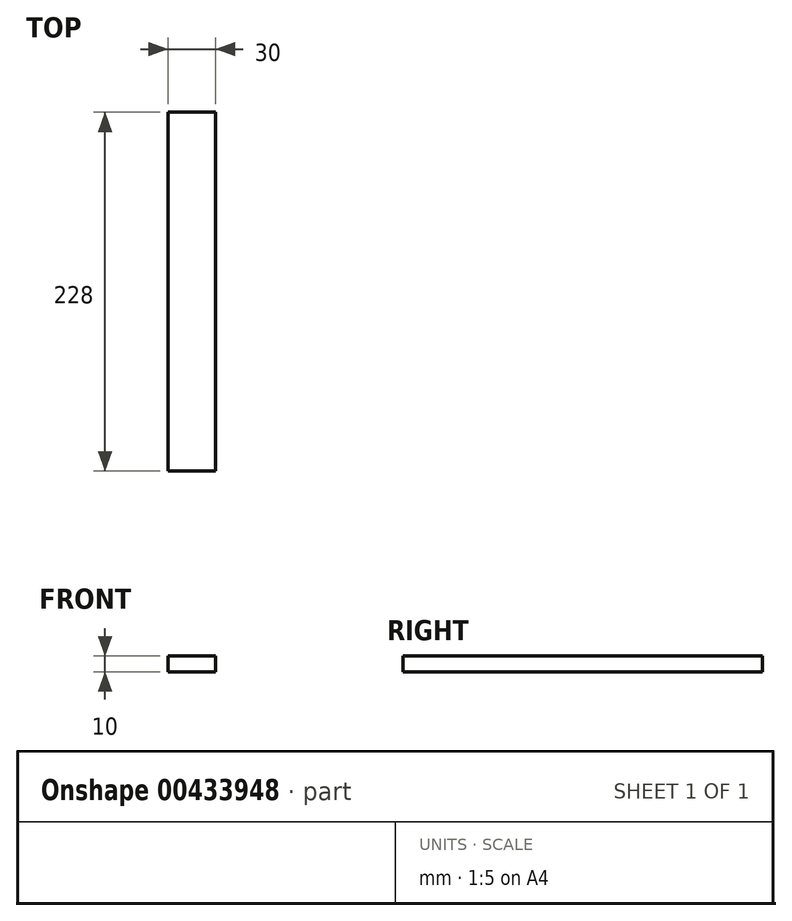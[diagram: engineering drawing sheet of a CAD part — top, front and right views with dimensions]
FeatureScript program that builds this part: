
annotation { "Feature Type Name" : "Feature", "Feature Type Description" : "" }
export const myFeature = defineFeature(function(context is Context, id is Id, definition is map)
    precondition{}
    {
        {
            var Q0;
            Q0=qCreatedBy(makeId("Top.planeOp"),FACE);
            var sketch = newSketch(context, id + "F0", { "sketchPlane" : qUnion([Q0])});
            skLineSegment(sketch, "E0.bottom", {"start": v(15, -114) * mm, "end": v(-15, -114) * mm});
            skLineSegment(sketch, "E0.top", {"start": v(15, 114) * mm, "end": v(-15, 114) * mm});
            skLineSegment(sketch, "E0.left", {"start": v(15, -114) * mm, "end": v(15, 114) * mm});
            skLineSegment(sketch, "E0.right", {"start": v(-15, -114) * mm, "end": v(-15, 114) * mm});
            skPoint(sketch, "E0.middle", {"position": v(0, 0) * mm});
            skSolve(sketch);
        }
        {
            var Q0;
            Q0 = qSketchRegion(id + "F0", true);
            extrude(context, id + "F1", {"entities" : qUnion([Q0]), "depth" : 10 * mm});
        }
    });
